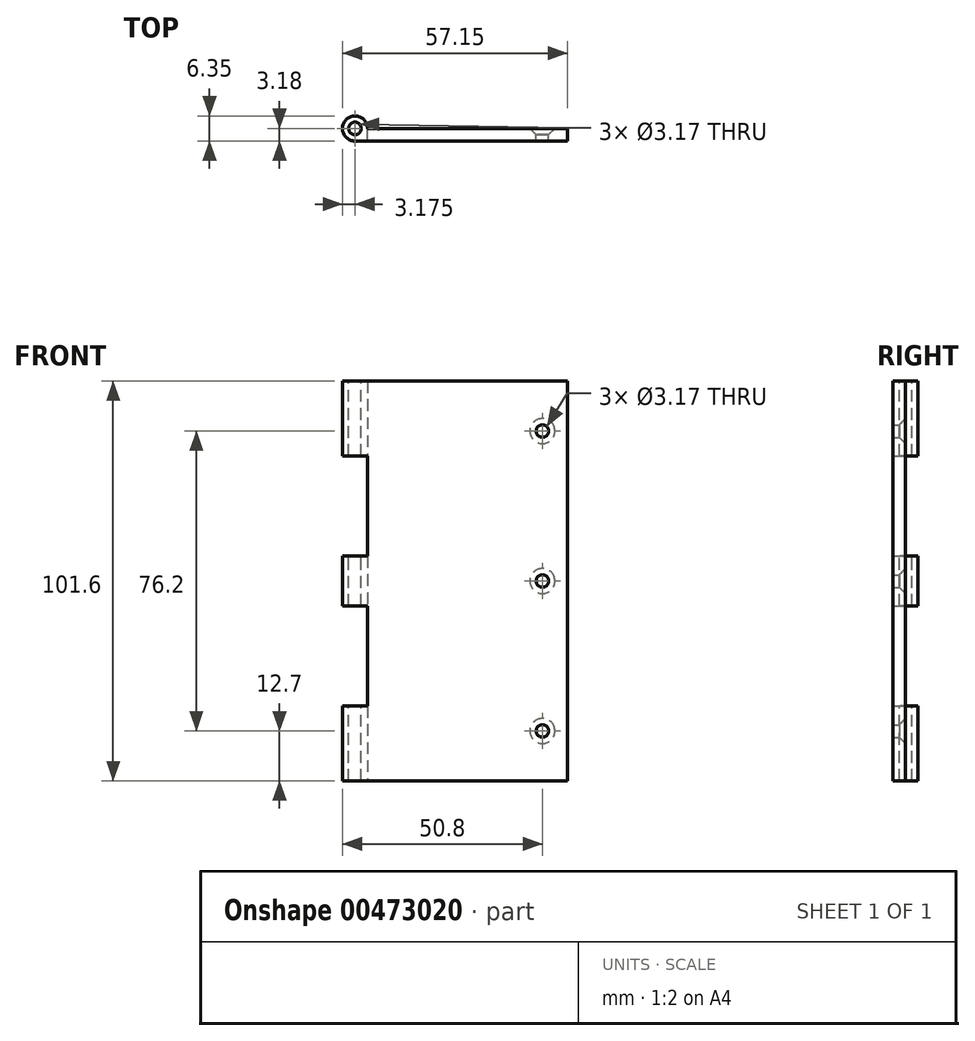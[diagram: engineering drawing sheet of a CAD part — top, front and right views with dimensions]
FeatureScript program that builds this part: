
annotation { "Feature Type Name" : "Feature", "Feature Type Description" : "" }
export const myFeature = defineFeature(function(context is Context, id is Id, definition is map)
    precondition{}
    {
        {
            var Q0;
            Q0=qCreatedBy(makeId("Front.planeOp"),FACE);
            var sketch = newSketch(context, id + "F0", { "sketchPlane" : qUnion([Q0])});
            skLineSegment(sketch, "E0.bottom", {"start": v(25.4, 50.8) * mm, "end": v(-25.4, 50.8) * mm});
            skLineSegment(sketch, "E0.top", {"start": v(25.4, -50.8) * mm, "end": v(-25.4, -50.8) * mm});
            skLineSegment(sketch, "E0.left", {"start": v(25.4, 50.8) * mm, "end": v(25.4, -50.8) * mm});
            skLineSegment(sketch, "E0.right", {"start": v(-25.4, 50.8) * mm, "end": v(-25.4, -50.8) * mm});
            skPoint(sketch, "E0.middle", {"position": v(0, 0) * mm});
            skSolve(sketch);
        }
        {
            var Q0;
            Q0=makeQuery(id+"F0.imprint","IMPRINT",FACE,{"disambiguationData":[TD([[makeQuery(id+"F0.imprint","IMPRINT",EDGE,{"derivedFrom":sQuery(id+"F0.wireOp",EDGE,"E0.bottom")}),1.0]])]});
            extrude(context, id + "F1", {"entities" : qUnion([Q0]), "depth" : 3.17 * mm});
        }
        {
            var Q0;
            Q0=makeQuery(id+"F1.opExtrude","SWEPT_FACE",FACE,{"disambiguationData":[OSD([sQuery(id+"F0.wireOp",EDGE,"E0.right")])]});
            var sketch = newSketch(context, id + "F2", { "sketchPlane" : qUnion([Q0])});
            skLineSegment(sketch, "E1.bottom", {"start": v(3.18, 50.8) * mm, "end": v(-3.18, 50.8) * mm});
            skLineSegment(sketch, "E1.top", {"start": v(3.18, 31.75) * mm, "end": v(-3.17, 31.75) * mm});
            skLineSegment(sketch, "E1.left", {"start": v(3.18, 50.8) * mm, "end": v(3.18, 31.75) * mm});
            skLineSegment(sketch, "E1.right", {"start": v(-3.18, 50.8) * mm, "end": v(-3.17, 31.75) * mm});
            skLineSegment(sketch, "E2.bottom", {"start": v(3.18, 6.35) * mm, "end": v(-3.17, 6.35) * mm});
            skLineSegment(sketch, "E2.top", {"start": v(3.18, -6.35) * mm, "end": v(-3.17, -6.35) * mm});
            skLineSegment(sketch, "E2.left", {"start": v(3.18, 6.35) * mm, "end": v(3.18, -6.35) * mm});
            skLineSegment(sketch, "E2.right", {"start": v(-3.17, 6.35) * mm, "end": v(-3.17, -6.35) * mm});
            skLineSegment(sketch, "E3.bottom", {"start": v(3.18, -50.8) * mm, "end": v(-3.17, -50.8) * mm});
            skLineSegment(sketch, "E3.top", {"start": v(3.17, -31.75) * mm, "end": v(-3.18, -31.75) * mm});
            skLineSegment(sketch, "E3.left", {"start": v(3.18, -50.8) * mm, "end": v(3.18, -31.75) * mm});
            skLineSegment(sketch, "E3.right", {"start": v(-3.17, -50.8) * mm, "end": v(-3.18, -31.75) * mm});
            skSolve(sketch);
        }
        {
            var Q0;
            {var subQ0=sQuery(id+"F2.wireOp",EDGE,"E2.right");Q0=makeQuery(id+"F2.imprint","IMPRINT",FACE,{"disambiguationData":[TD([[makeQuery(id+"F2.imprint","IMPRINT",EDGE,{"derivedFrom":subQ0}),1.0]])]});}
            var Q1;
            {var subQ3=sQuery(id+"F2.wireOp",EDGE,"E3.right");Q1=makeQuery(id+"F2.imprint","IMPRINT",FACE,{"disambiguationData":[TD([[makeQuery(id+"F2.imprint","IMPRINT",EDGE,{"derivedFrom":subQ3}),-1.0]])]});}
            var Q2;
            {var subQ4=sQuery(id+"F2.wireOp",EDGE,"E1.left");Q2=makeQuery(id+"F2.imprint","IMPRINT",FACE,{"disambiguationData":[TD([[makeQuery(id+"F2.imprint","IMPRINT",EDGE,{"derivedFrom":subQ4}),-1.0]])]});}
            var Q3;
            {var subQ4=sQuery(id+"F2.wireOp",EDGE,"E3.left");Q3=makeQuery(id+"F2.imprint","IMPRINT",FACE,{"disambiguationData":[TD([[makeQuery(id+"F2.imprint","IMPRINT",EDGE,{"derivedFrom":subQ4}),-1.0]])]});}
            var Q4;
            {var subQ0=sQuery(id+"F2.wireOp",EDGE,"E2.left");Q4=makeQuery(id+"F2.imprint","IMPRINT",FACE,{"disambiguationData":[TD([[makeQuery(id+"F2.imprint","IMPRINT",EDGE,{"derivedFrom":subQ0}),-1.0]])]});}
            var Q5;
            {var subQ3=sQuery(id+"F2.wireOp",EDGE,"E1.right");Q5=makeQuery(id+"F2.imprint","IMPRINT",FACE,{"disambiguationData":[TD([[makeQuery(id+"F2.imprint","IMPRINT",EDGE,{"derivedFrom":subQ3}),1.0]])]});}
            extrude(context, id + "F3", {"entities" : qUnion([Q0, Q1, Q2, Q3, Q4, Q5]), "operationType" : NewBodyOperationType.ADD, "depth" : 6.35 * mm});
        }
        {
            var Q0;
            Q0=makeQuery(id+"F3.boolean.opBoolean","MERGE",FACE,{"derivedFrom":[makeQuery(id+"F1.opExtrude","SWEPT_FACE",FACE,{"disambiguationData":[OSD([sQuery(id+"F0.wireOp",EDGE,"E0.bottom")])]}),makeQuery(id+"F3.opExtrude","SWEPT_FACE",FACE,{"disambiguationData":[OSD([sQuery(id+"F2.wireOp",EDGE,"E1.bottom")])]})]});
            var sketch = newSketch(context, id + "F4", { "sketchPlane" : qUnion([Q0])});
            skCircle(sketch, "E4", {"center": v(-28.58, 0) * mm, "radius": 3.18 * mm});
            skPoint(sketch, "E4.centerSnap0", {"position": v(-28.58, 3.18) * mm});
            skPoint(sketch, "E4.centerSnap1", {"position": v(-31.75, 0) * mm});
            skSolve(sketch);
        }
        {
            var Q0;
            {var subQ0=sQuery(id+"F4.wireOp",EDGE,"E4");var subQ1=sQuery(id+"F2.wireOp",EDGE,"E1.bottom");var subQ4=makeQuery(id+"F3.opExtrude","CAP_EDGE",EDGE,{"disambiguationData":[OSD([subQ1])],"isStart":false});var subQ5=makeQuery(id+"F4.imprint","INTERSECT",VERTEX,{"derivedFrom":[subQ4,subQ0]});Q0=makeQuery(id+"F4.imprint","IMPRINT",FACE,{"disambiguationData":[TD([[makeQuery(id+"F4.imprint","IMPRINT",EDGE,{"disambiguationData":[TD([[subQ5,1.0]])],"derivedFrom":subQ0}),-1.0]])]});}
            var Q1;
            {var subQ1=sQuery(id+"F2.wireOp",EDGE,"E1.bottom");var subQ2=makeQuery(id+"F3.opExtrude","CAP_EDGE",EDGE,{"disambiguationData":[OSD([subQ1])],"isStart":true});Q1=makeQuery(id+"F4.imprint","IMPRINT",FACE,{"disambiguationData":[TD([[makeQuery(id+"F4.imprint","IMPRINT",EDGE,{"derivedFrom":subQ2}),1.0]])]});}
            var Q2;
            {var subQ0=sQuery(id+"F4.wireOp",EDGE,"E4");var subQ1=sQuery(id+"F2.wireOp",EDGE,"E1.bottom");var subQ2=makeQuery(id+"F3.opExtrude","CAP_EDGE",EDGE,{"disambiguationData":[OSD([subQ1])],"isStart":false});var subQ3=makeQuery(id+"F4.imprint","INTERSECT",VERTEX,{"derivedFrom":[subQ2,subQ0]});Q2=makeQuery(id+"F4.imprint","IMPRINT",FACE,{"disambiguationData":[TD([[makeQuery(id+"F4.imprint","IMPRINT",EDGE,{"disambiguationData":[TD([[subQ3,-1.0]])],"derivedFrom":subQ0}),-1.0]])]});}
            extrude(context, id + "F5", {"entities" : qUnion([Q0, Q1, Q2]), "operationType" : NewBodyOperationType.REMOVE, "endBound" : BoundingType.THROUGH_ALL, "oppositeDirection" : true, "depth" : 25.4 * mm});
        }
        {
            var Q0;
            Q0=makeQuery(id+"F3.boolean.opBoolean","MERGE",FACE,{"derivedFrom":[makeQuery(id+"F1.opExtrude","SWEPT_FACE",FACE,{"disambiguationData":[OSD([sQuery(id+"F0.wireOp",EDGE,"E0.bottom")])]}),makeQuery(id+"F3.opExtrude","SWEPT_FACE",FACE,{"disambiguationData":[OSD([sQuery(id+"F2.wireOp",EDGE,"E1.bottom")])]})]});
            var sketch = newSketch(context, id + "F6", { "sketchPlane" : qUnion([Q0])});
            skCircle(sketch, "E5", {"center": v(-28.58, 0) * mm, "radius": 1.59 * mm});
            skSolve(sketch);
        }
        {
            var Q0;
            Q0=makeQuery(id+"F6.imprint","IMPRINT",FACE,{"disambiguationData":[TD([[makeQuery(id+"F6.imprint","IMPRINT",EDGE,{"derivedFrom":sQuery(id+"F6.wireOp",EDGE,"E5")}),1.0]])]});
            extrude(context, id + "F7", {"entities" : qUnion([Q0]), "operationType" : NewBodyOperationType.REMOVE, "endBound" : BoundingType.THROUGH_ALL, "oppositeDirection" : true, "depth" : 25.4 * mm});
        }
        {
            var Q0;
            Q0=makeQuery(id+"F1.opExtrude","CAP_FACE",FACE,{"disambiguationData":[OSD([sQuery(id+"F0.wireOp",EDGE,"E0.bottom"),sQuery(id+"F0.wireOp",EDGE,"E0.top"),sQuery(id+"F0.wireOp",EDGE,"E0.left"),sQuery(id+"F0.wireOp",EDGE,"E0.right")])],"isStart":true});
            var sketch = newSketch(context, id + "F8", { "sketchPlane" : qUnion([Q0])});
            skCircle(sketch, "E6", {"center": v(-19.05, 38.1) * mm, "radius": 1.59 * mm});
            skCircle(sketch, "E7", {"center": v(-19.05, 0) * mm, "radius": 1.59 * mm});
            skCircle(sketch, "E8", {"center": v(-19.05, -38.1) * mm, "radius": 1.59 * mm});
            skSolve(sketch);
        }
        {
            var Q0;
            Q0=sQuery(id+"F8.wireOp",VERTEX,"E6.center");
            var Q1;
            Q1=sQuery(id+"F8.wireOp",VERTEX,"E7.center");
            var Q2;
            Q2=sQuery(id+"F8.wireOp",VERTEX,"E8.center");
            var Q3;
            Q3=makeQuery(id+"F1.opExtrude","SWEPT_BODY",BODY,{"disambiguationData":[OSD([sQuery(id+"F0.wireOp",EDGE,"E0.bottom"),sQuery(id+"F0.wireOp",EDGE,"E0.top"),sQuery(id+"F0.wireOp",EDGE,"E0.left"),sQuery(id+"F0.wireOp",EDGE,"E0.right")])]});
            hole(context, id + "F9", {"style" : HoleStyle.C_SINK, "endStyle" : HoleEndStyle.THROUGH, "holeDiameter" : 3.17 * mm, "cSinkDiameter" : 6.35 * mm, "cSinkAngle" : 90 * degree, "isTappedThrough" : true, "tappedDepth" : 12.7 * mm, "tapClearance" : 3, "locations" : qUnion([Q0, Q1, Q2]), "scope" : qUnion([Q3])});
        }
    });
